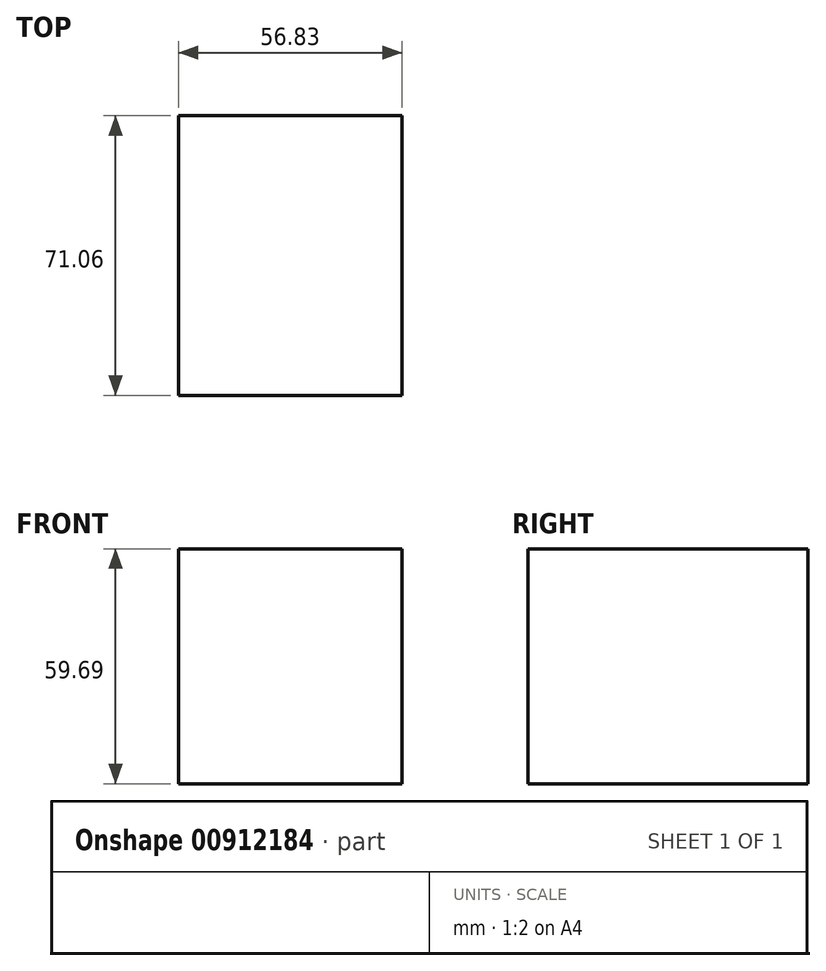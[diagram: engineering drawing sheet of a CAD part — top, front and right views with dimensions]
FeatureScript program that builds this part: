
annotation { "Feature Type Name" : "Feature", "Feature Type Description" : "" }
export const myFeature = defineFeature(function(context is Context, id is Id, definition is map)
    precondition{}
    {
        {
            var Q0;
            Q0=qCreatedBy(makeId("Top.planeOp"),FACE);
            var sketch = newSketch(context, id + "F0", { "sketchPlane" : qUnion([Q0])});
            skLineSegment(sketch, "E0.bottom", {"start": v(0, 0) * mm, "end": v(56.83, 0) * mm});
            skLineSegment(sketch, "E0.top", {"start": v(0, 71.06) * mm, "end": v(56.83, 71.06) * mm});
            skLineSegment(sketch, "E0.left", {"start": v(0, 0) * mm, "end": v(0, 71.06) * mm});
            skLineSegment(sketch, "E0.right", {"start": v(56.83, 0) * mm, "end": v(56.83, 71.06) * mm});
            skSolve(sketch);
        }
        {
            var Q0;
            Q0=makeQuery(id+"F0.imprint","IMPRINT",FACE,{"disambiguationData":[TD([[makeQuery(id+"F0.imprint","IMPRINT",EDGE,{"derivedFrom":sQuery(id+"F0.wireOp",EDGE,"E0.bottom")}),1.0]])]});
            extrude(context, id + "F1", {"entities" : qUnion([Q0]), "depth" : 59.69 * mm, "offsetDistance" : 25.4 * mm});
        }
    });
